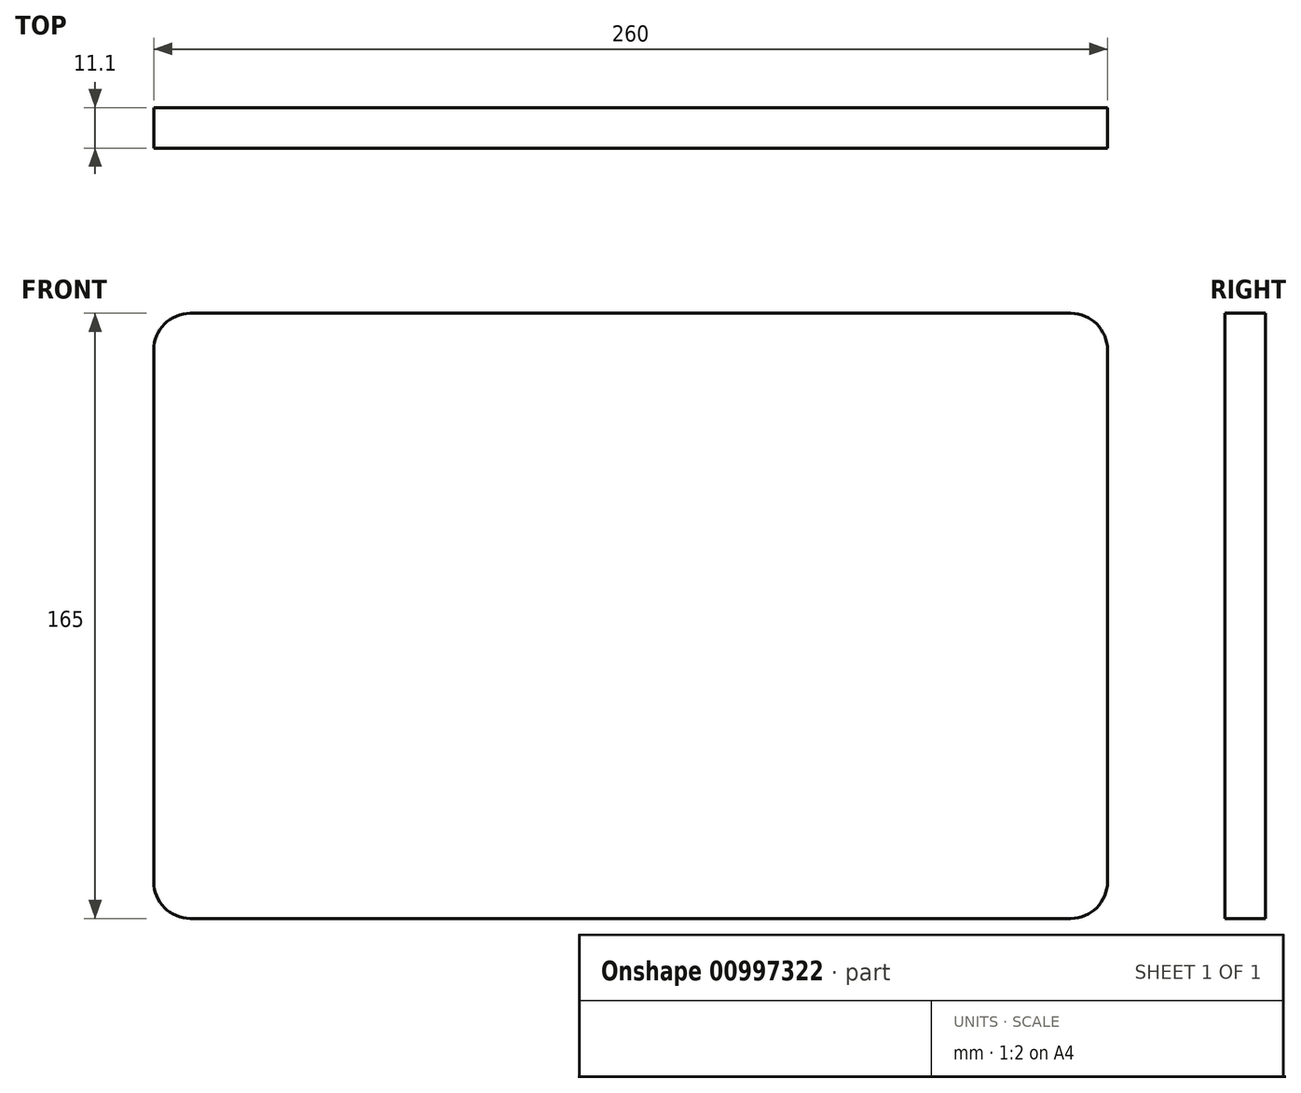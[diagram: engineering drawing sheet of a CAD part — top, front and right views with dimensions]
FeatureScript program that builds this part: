
annotation { "Feature Type Name" : "Feature", "Feature Type Description" : "" }
export const myFeature = defineFeature(function(context is Context, id is Id, definition is map)
    precondition{}
    {
        {
            var Q0;
            Q0=qCreatedBy(makeId("Front.planeOp"),FACE);
            var sketch = newSketch(context, id + "F0", { "sketchPlane" : qUnion([Q0])});
            skLineSegment(sketch, "E0.bottom", {"start": v(130, -82.5) * mm, "end": v(-130, -82.5) * mm});
            skLineSegment(sketch, "E0.top", {"start": v(130, 82.5) * mm, "end": v(-130, 82.5) * mm});
            skLineSegment(sketch, "E0.left", {"start": v(130, -82.5) * mm, "end": v(130, 82.5) * mm});
            skLineSegment(sketch, "E0.right", {"start": v(-130, -82.5) * mm, "end": v(-130, 82.5) * mm});
            skPoint(sketch, "E0.middle", {"position": v(0, 0) * mm});
            skSolve(sketch);
        }
        {
            var Q0;
            Q0=qSketchRegion(id+"F0",true);
            extrude(context, id + "F1", {"entities" : qUnion([Q0]), "depth" : 11.1 * mm, "offsetDistance" : 25.4 * mm});
        }
        {
            var Q0;
            Q0=makeQuery(id+"F1.opExtrude","SWEPT_EDGE",EDGE,{"disambiguationData":[OSD([sQuery(id+"F0.wireOp",EDGE,"E0.bottom"),sQuery(id+"F0.wireOp",EDGE,"E0.right")])]});
            var Q1;
            Q1=makeQuery(id+"F1.opExtrude","SWEPT_EDGE",EDGE,{"disambiguationData":[OSD([sQuery(id+"F0.wireOp",EDGE,"E0.bottom"),sQuery(id+"F0.wireOp",EDGE,"E0.left")])]});
            var Q2;
            Q2=makeQuery(id+"F1.opExtrude","SWEPT_EDGE",EDGE,{"disambiguationData":[OSD([sQuery(id+"F0.wireOp",EDGE,"E0.top"),sQuery(id+"F0.wireOp",EDGE,"E0.left")])]});
            var Q3;
            Q3=makeQuery(id+"F1.opExtrude","SWEPT_EDGE",EDGE,{"disambiguationData":[OSD([sQuery(id+"F0.wireOp",EDGE,"E0.top"),sQuery(id+"F0.wireOp",EDGE,"E0.right")])]});
            fillet(context, id + "F2", {"entities" : qUnion([Q0, Q1, Q2, Q3]), "radius" : 10 * mm, "tangentPropagation" : true, "allowEdgeOverflow" : false});
        }
    });
